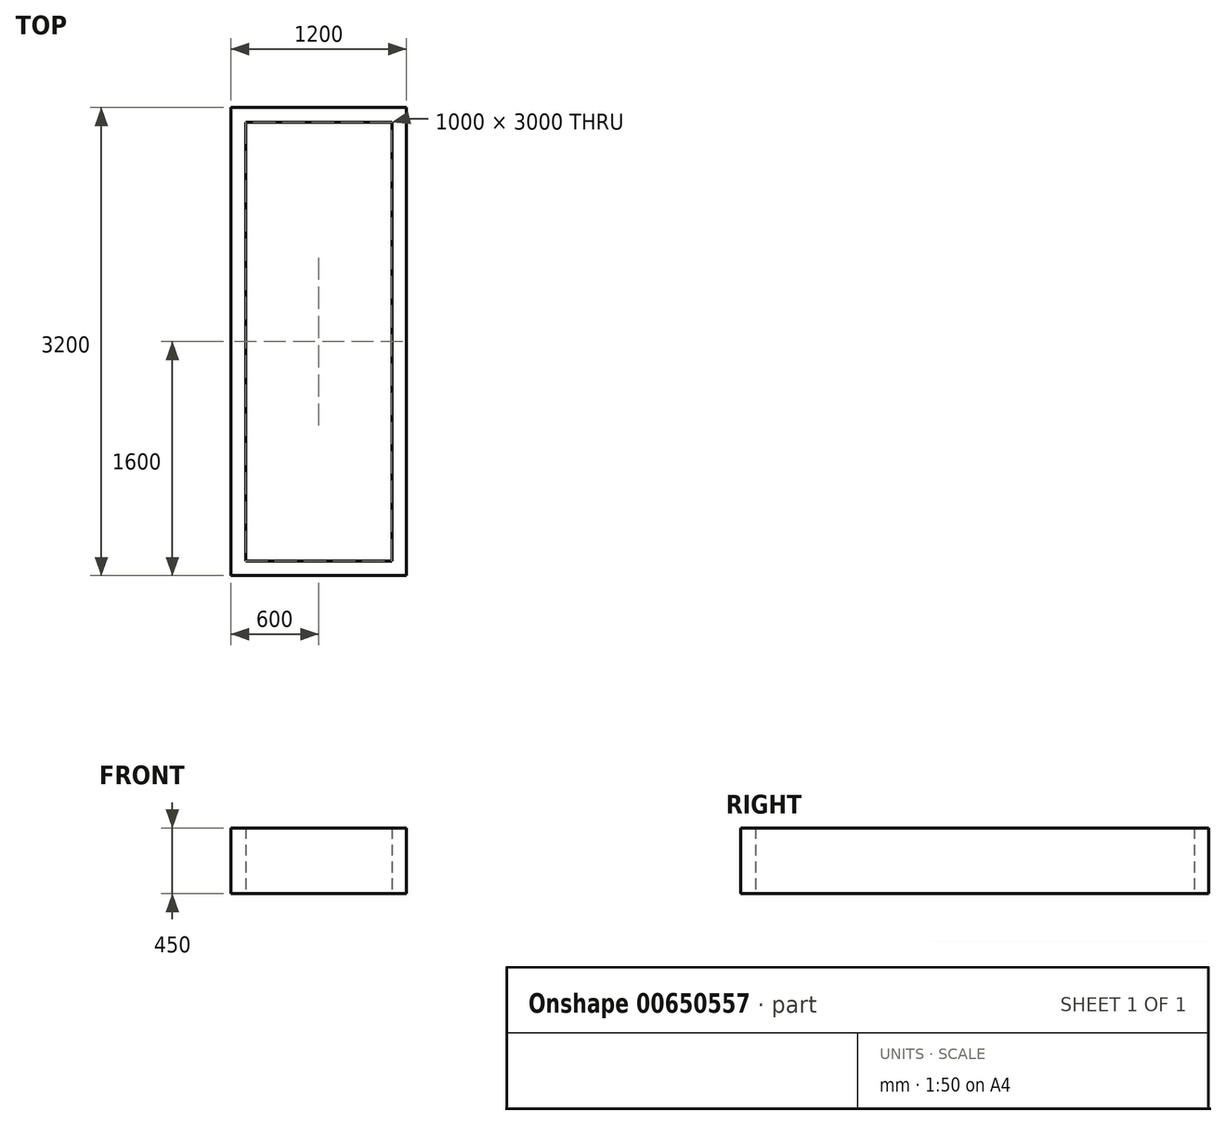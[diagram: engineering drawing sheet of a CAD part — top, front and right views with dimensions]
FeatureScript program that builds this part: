
annotation { "Feature Type Name" : "Feature", "Feature Type Description" : "" }
export const myFeature = defineFeature(function(context is Context, id is Id, definition is map)
    precondition{}
    {
        {
            var Q0;
            Q0=qCreatedBy(makeId("Top.planeOp"),FACE);
            var sketch = newSketch(context, id + "F0", { "sketchPlane" : qUnion([Q0]), "disableImprinting" : false});
            skLineSegment(sketch, "E0.bottom", {"start": v(0, 0) * mm, "end": v(-1200, 0) * mm});
            skLineSegment(sketch, "E0.top", {"start": v(0, 3200) * mm, "end": v(-1200, 3200) * mm});
            skLineSegment(sketch, "E0.left", {"start": v(0, 0) * mm, "end": v(0, 3200) * mm});
            skLineSegment(sketch, "E0.right", {"start": v(-1200, 0) * mm, "end": v(-1200, 3200) * mm});
            skLineSegment(sketch, "E1.bottom", {"start": v(-100, 100) * mm, "end": v(-1100, 100) * mm});
            skLineSegment(sketch, "E1.top", {"start": v(-100, 3100) * mm, "end": v(-1100, 3100) * mm});
            skLineSegment(sketch, "E1.left", {"start": v(-100, 100) * mm, "end": v(-100, 3100) * mm});
            skLineSegment(sketch, "E1.right", {"start": v(-1100, 100) * mm, "end": v(-1100, 3100) * mm});
            skSolve(sketch);
        }
        {
            var Q0;
            Q0 = qSketchRegion(id + "F0", true);
            extrude(context, id + "F1", {"entities" : qUnion([Q0]), "flatOperationType" : FlatOperationType.REMOVE, "thickness1" : 5 * mm, "thickness2" : 0 * mm, "thickness" : 5 * mm, "depth" : 450 * mm, "offsetDistance" : 25 * mm, "startOffsetBound" : StartOffsetType.BLIND, "startOffsetDistance" : 25 * mm, "domain" : OperationDomain.MODEL});
        }
    });
